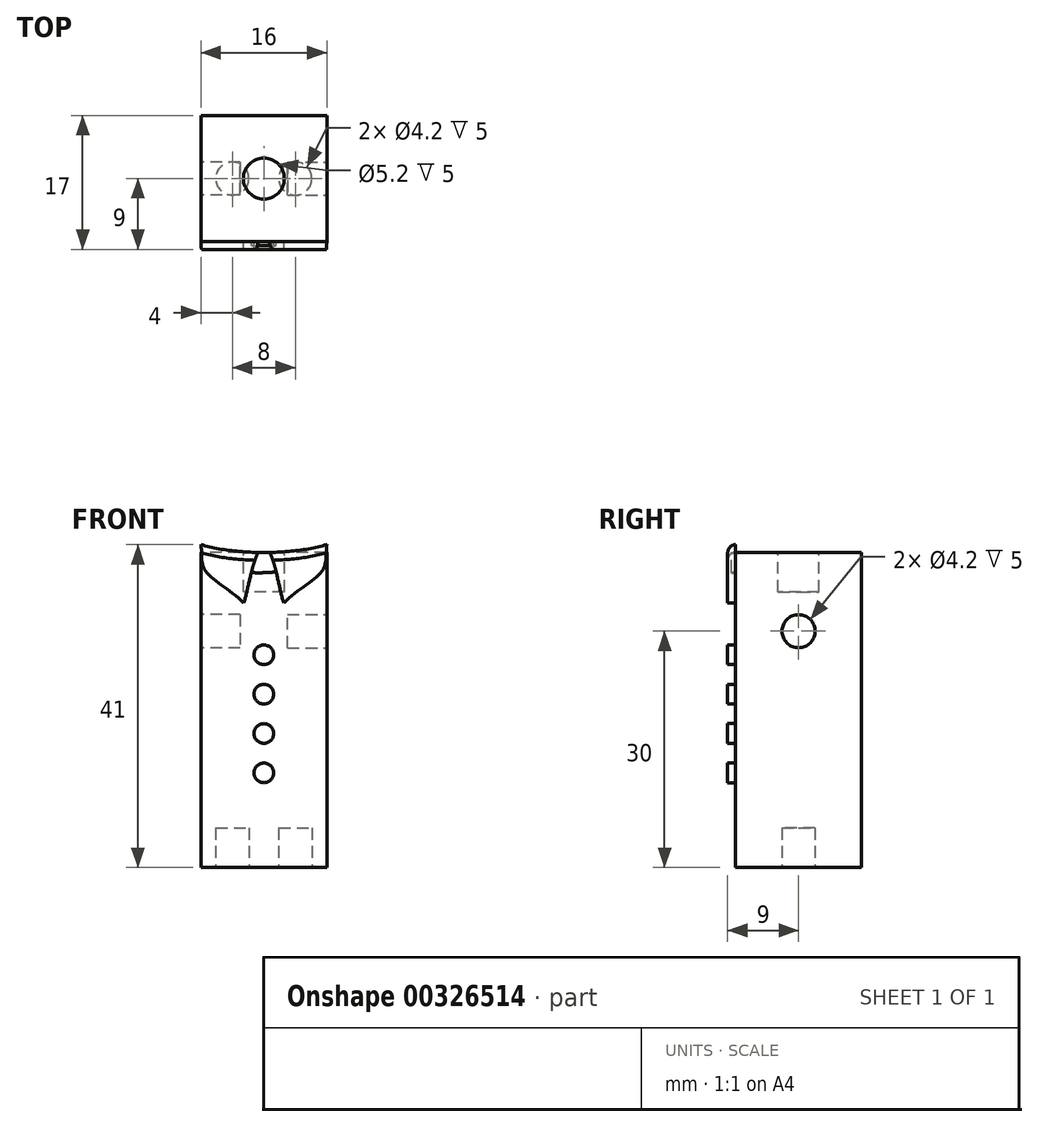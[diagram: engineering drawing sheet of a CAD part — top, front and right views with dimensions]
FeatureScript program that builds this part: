
annotation { "Feature Type Name" : "Feature", "Feature Type Description" : "" }
export const myFeature = defineFeature(function(context is Context, id is Id, definition is map)
    precondition{}
    {
        {
            var Q0;
            Q0=qCreatedBy(makeId("Front.planeOp"),FACE);
            var sketch = newSketch(context, id + "F0", { "sketchPlane" : qUnion([Q0])});
            skLineSegment(sketch, "E0.bottom", {"start": v(8, 20) * mm, "end": v(-8, 20) * mm});
            skLineSegment(sketch, "E0.top", {"start": v(8, -20) * mm, "end": v(-8, -20) * mm});
            skLineSegment(sketch, "E0.left", {"start": v(8, 20) * mm, "end": v(8, -20) * mm});
            skLineSegment(sketch, "E0.right", {"start": v(-8, 20) * mm, "end": v(-8, -20) * mm});
            skPoint(sketch, "E0.middle", {"position": v(0, 0) * mm});
            skSolve(sketch);
        }
        {
            var Q0;
            Q0=makeQuery(id+"F0.imprint","IMPRINT",FACE,{"disambiguationData":[TD([[makeQuery(id+"F0.imprint","IMPRINT",EDGE,{"derivedFrom":sQuery(id+"F0.wireOp",EDGE,"E0.bottom")}),1.0]])]});
            extrude(context, id + "F1", {"entities" : qUnion([Q0]), "depth" : 16 * mm});
        }
        {
            var Q0;
            Q0=makeQuery(id+"F1.opExtrude","SWEPT_FACE",FACE,{"disambiguationData":[OSD([sQuery(id+"F0.wireOp",EDGE,"E0.bottom")])]});
            var sketch = newSketch(context, id + "F2", { "sketchPlane" : qUnion([Q0])});
            skCircle(sketch, "E1", {"center": v(0, -8) * mm, "radius": 2.6 * mm});
            skSolve(sketch);
        }
        {
            var Q0;
            Q0=makeQuery(id+"F2.imprint","IMPRINT",FACE,{"disambiguationData":[TD([[makeQuery(id+"F2.imprint","IMPRINT",EDGE,{"derivedFrom":sQuery(id+"F2.wireOp",EDGE,"E1")}),1.0]])]});
            extrude(context, id + "F3", {"entities" : qUnion([Q0]), "operationType" : NewBodyOperationType.REMOVE, "oppositeDirection" : true, "depth" : 5 * mm});
        }
        {
            var Q0;
            Q0=makeQuery(id+"F1.opExtrude","SWEPT_FACE",FACE,{"disambiguationData":[OSD([sQuery(id+"F0.wireOp",EDGE,"E0.left")])]});
            var sketch = newSketch(context, id + "F4", { "sketchPlane" : qUnion([Q0])});
            skCircle(sketch, "E2", {"center": v(-8, 10) * mm, "radius": 2.1 * mm});
            skSolve(sketch);
        }
        {
            var Q0;
            Q0=makeQuery(id+"F4.imprint","IMPRINT",FACE,{"disambiguationData":[TD([[makeQuery(id+"F4.imprint","IMPRINT",EDGE,{"derivedFrom":sQuery(id+"F4.wireOp",EDGE,"E2")}),1.0]])]});
            extrude(context, id + "F5", {"entities" : qUnion([Q0]), "operationType" : NewBodyOperationType.REMOVE, "oppositeDirection" : true, "depth" : 5 * mm});
        }
        {
            var Q0;
            Q0=makeQuery(id+"F1.opExtrude","SWEPT_FACE",FACE,{"disambiguationData":[OSD([sQuery(id+"F0.wireOp",EDGE,"E0.right")])]});
            var sketch = newSketch(context, id + "F6", { "sketchPlane" : qUnion([Q0])});
            skCircle(sketch, "E3", {"center": v(8, 10) * mm, "radius": 2.1 * mm});
            skSolve(sketch);
        }
        {
            var Q0;
            Q0=makeQuery(id+"F6.imprint","IMPRINT",FACE,{"disambiguationData":[TD([[makeQuery(id+"F6.imprint","IMPRINT",EDGE,{"derivedFrom":sQuery(id+"F6.wireOp",EDGE,"E3")}),1.0]])]});
            extrude(context, id + "F7", {"entities" : qUnion([Q0]), "operationType" : NewBodyOperationType.REMOVE, "oppositeDirection" : true, "depth" : 5 * mm});
        }
        {
            var Q0;
            Q0=makeQuery(id+"F1.opExtrude","SWEPT_FACE",FACE,{"disambiguationData":[OSD([sQuery(id+"F0.wireOp",EDGE,"E0.top")])]});
            var sketch = newSketch(context, id + "F8", { "sketchPlane" : qUnion([Q0])});
            skCircle(sketch, "E4", {"center": v(4, 8) * mm, "radius": 2.1 * mm});
            skSolve(sketch);
        }
        {
            var Q0;
            Q0=makeQuery(id+"F8.imprint","IMPRINT",FACE,{"disambiguationData":[TD([[makeQuery(id+"F8.imprint","IMPRINT",EDGE,{"derivedFrom":sQuery(id+"F8.wireOp",EDGE,"E4")}),1.0]])]});
            extrude(context, id + "F9", {"entities" : qUnion([Q0]), "operationType" : NewBodyOperationType.REMOVE, "oppositeDirection" : true, "depth" : 5 * mm});
        }
        {
            var Q0;
            Q0=makeQuery(id+"F1.opExtrude","SWEPT_FACE",FACE,{"disambiguationData":[OSD([sQuery(id+"F0.wireOp",EDGE,"E0.top")])]});
            var sketch = newSketch(context, id + "F10", { "sketchPlane" : qUnion([Q0])});
            skCircle(sketch, "E5", {"center": v(-4, 8) * mm, "radius": 2.1 * mm});
            skSolve(sketch);
        }
        {
            var Q0;
            Q0=makeQuery(id+"F10.imprint","IMPRINT",FACE,{"disambiguationData":[TD([[makeQuery(id+"F10.imprint","IMPRINT",EDGE,{"derivedFrom":sQuery(id+"F10.wireOp",EDGE,"E5")}),1.0]])]});
            extrude(context, id + "F11", {"entities" : qUnion([Q0]), "operationType" : NewBodyOperationType.REMOVE, "oppositeDirection" : true, "depth" : 5 * mm});
        }
        {
            var Q0;
            Q0=makeQuery(id+"F1.opExtrude","CAP_FACE",FACE,{"disambiguationData":[OSD([sQuery(id+"F0.wireOp",EDGE,"E0.bottom"),sQuery(id+"F0.wireOp",EDGE,"E0.top"),sQuery(id+"F0.wireOp",EDGE,"E0.left"),sQuery(id+"F0.wireOp",EDGE,"E0.right")])],"isStart":false});
            var sketch = newSketch(context, id + "F12", { "sketchPlane" : qUnion([Q0])});
            skCircle(sketch, "E6", {"center": v(0, 7) * mm, "radius": 1.25 * mm});
            skSolve(sketch);
        }
        {
            var Q0;
            Q0=makeQuery(id+"F12.imprint","IMPRINT",FACE,{"disambiguationData":[TD([[makeQuery(id+"F12.imprint","IMPRINT",EDGE,{"derivedFrom":sQuery(id+"F12.wireOp",EDGE,"E6")}),1.0]])]});
            extrude(context, id + "F13", {"entities" : qUnion([Q0]), "operationType" : NewBodyOperationType.ADD, "depth" : 1 * mm});
        }
        {
            var Q0;
            Q0=makeQuery(id+"F1.opExtrude","CAP_FACE",FACE,{"disambiguationData":[OSD([sQuery(id+"F0.wireOp",EDGE,"E0.bottom"),sQuery(id+"F0.wireOp",EDGE,"E0.top"),sQuery(id+"F0.wireOp",EDGE,"E0.left"),sQuery(id+"F0.wireOp",EDGE,"E0.right")])],"isStart":false});
            var sketch = newSketch(context, id + "F14", { "sketchPlane" : qUnion([Q0])});
            skCircle(sketch, "E7", {"center": v(0, 2) * mm, "radius": 1.25 * mm});
            skSolve(sketch);
        }
        {
            var Q0;
            Q0=makeQuery(id+"F14.imprint","IMPRINT",FACE,{"disambiguationData":[TD([[makeQuery(id+"F14.imprint","IMPRINT",EDGE,{"derivedFrom":sQuery(id+"F14.wireOp",EDGE,"E7")}),1.0]])]});
            extrude(context, id + "F15", {"entities" : qUnion([Q0]), "operationType" : NewBodyOperationType.ADD, "depth" : 1 * mm});
        }
        {
            var Q0;
            Q0=makeQuery(id+"F1.opExtrude","CAP_FACE",FACE,{"disambiguationData":[OSD([sQuery(id+"F0.wireOp",EDGE,"E0.bottom"),sQuery(id+"F0.wireOp",EDGE,"E0.top"),sQuery(id+"F0.wireOp",EDGE,"E0.left"),sQuery(id+"F0.wireOp",EDGE,"E0.right")])],"isStart":false});
            var sketch = newSketch(context, id + "F16", { "sketchPlane" : qUnion([Q0])});
            skCircle(sketch, "E8", {"center": v(0, -3) * mm, "radius": 1.25 * mm});
            skSolve(sketch);
        }
        {
            var Q0;
            Q0=makeQuery(id+"F16.imprint","IMPRINT",FACE,{"disambiguationData":[TD([[makeQuery(id+"F16.imprint","IMPRINT",EDGE,{"derivedFrom":sQuery(id+"F16.wireOp",EDGE,"E8")}),1.0]])]});
            extrude(context, id + "F17", {"entities" : qUnion([Q0]), "operationType" : NewBodyOperationType.ADD, "depth" : 1 * mm});
        }
        {
            var Q0;
            Q0=makeQuery(id+"F1.opExtrude","CAP_FACE",FACE,{"disambiguationData":[OSD([sQuery(id+"F0.wireOp",EDGE,"E0.bottom"),sQuery(id+"F0.wireOp",EDGE,"E0.top"),sQuery(id+"F0.wireOp",EDGE,"E0.left"),sQuery(id+"F0.wireOp",EDGE,"E0.right")])],"isStart":false});
            var sketch = newSketch(context, id + "F18", { "sketchPlane" : qUnion([Q0])});
            skCircle(sketch, "E9", {"center": v(0, -8) * mm, "radius": 1.25 * mm});
            skSolve(sketch);
        }
        {
            var Q0;
            Q0=makeQuery(id+"F18.imprint","IMPRINT",FACE,{"disambiguationData":[TD([[makeQuery(id+"F18.imprint","IMPRINT",EDGE,{"derivedFrom":sQuery(id+"F18.wireOp",EDGE,"E9")}),1.0]])]});
            extrude(context, id + "F19", {"entities" : qUnion([Q0]), "operationType" : NewBodyOperationType.ADD, "depth" : 1 * mm});
        }
        {
            var Q0;
            Q0=makeQuery(id+"F1.opExtrude","CAP_FACE",FACE,{"disambiguationData":[OSD([sQuery(id+"F0.wireOp",EDGE,"E0.bottom"),sQuery(id+"F0.wireOp",EDGE,"E0.top"),sQuery(id+"F0.wireOp",EDGE,"E0.left"),sQuery(id+"F0.wireOp",EDGE,"E0.right")])],"isStart":false});
            var sketch = newSketch(context, id + "F20", { "sketchPlane" : qUnion([Q0])});
            skFitSpline(sketch, "E10", {"points": [v(-8, 21) * mm, v(8, 21) * mm], "startDerivative": vector(13.44, -4) * mm, "endDerivative": vector(13.65, 4.05) * mm});
            skFitSpline(sketch, "E11", {"points": [v(-8, 21) * mm, v(-7.6, 17.96) * mm, v(-2.55, 13.56) * mm], "startDerivative": vector(1.28, -6.23) * mm, "endDerivative": vector(8.93, -9.49) * mm});
            skFitSpline(sketch, "E12", {"points": [v(-2.55, 13.56) * mm, v(-0.75, 20) * mm], "startDerivative": vector(1.8, 6.04) * mm, "endDerivative": vector(2.7, 6.14) * mm});
            skFitSpline(sketch, "E13", {"points": [v(8, 21) * mm, v(7.59, 17.96) * mm, v(2.55, 13.56) * mm], "startDerivative": vector(-1.33, -6.24) * mm, "endDerivative": vector(-8.37, -9.42) * mm});
            skFitSpline(sketch, "E14", {"points": [v(2.55, 13.56) * mm, v(0.75, 20) * mm], "startDerivative": vector(-2.09, 6.11) * mm, "endDerivative": vector(-2.78, 5.88) * mm});
            skFitSpline(sketch, "E15", {"points": [v(-1.59, 17.47) * mm, v(1.57, 17.52) * mm], "startDerivative": vector(2.83, -0.35) * mm, "endDerivative": vector(2.9, 0.15) * mm});
            skPoint(sketch, "E16.centerSnap0", {"position": v(0, 20) * mm});
            skPoint(sketch, "E17", {"position": v(7.93, 20) * mm});
            skSolve(sketch);
        }
        {
            var Q0;
            {var subQ0=sQuery(id+"F20.wireOp",EDGE,"E13");var subQ1=sQuery(id+"F20.wireOp",EDGE,"E10");var subQ2=makeQuery(id+"F20.imprint","INTERSECT",VERTEX,{"derivedFrom":[subQ1,subQ0]});Q0=makeQuery(id+"F20.imprint","IMPRINT",FACE,{"disambiguationData":[TD([[makeQuery(id+"F20.imprint","IMPRINT",EDGE,{"disambiguationData":[TD([[subQ2,-1.0]])],"derivedFrom":subQ0}),-1.0]])]});}
            var Q1;
            {var subQ0=sQuery(id+"F20.wireOp",EDGE,"E11");var subQ1=sQuery(id+"F20.wireOp",EDGE,"E10");var subQ2=makeQuery(id+"F20.imprint","INTERSECT",VERTEX,{"derivedFrom":[subQ1,subQ0]});Q1=makeQuery(id+"F20.imprint","IMPRINT",FACE,{"disambiguationData":[TD([[makeQuery(id+"F20.imprint","IMPRINT",EDGE,{"disambiguationData":[TD([[subQ2,-1.0]])],"derivedFrom":subQ0}),1.0]])]});}
            var Q2;
            {var subQ0=sQuery(id+"F20.wireOp",EDGE,"E14");var subQ1=sQuery(id+"F20.wireOp",EDGE,"E13");var subQ2=makeQuery(id+"F20.imprint","INTERSECT",VERTEX,{"derivedFrom":[subQ1,subQ0]});Q2=makeQuery(id+"F20.imprint","IMPRINT",FACE,{"disambiguationData":[TD([[makeQuery(id+"F20.imprint","IMPRINT",EDGE,{"disambiguationData":[TD([[subQ2,1.0]])],"derivedFrom":subQ1}),-1.0]])]});}
            var Q3;
            {var subQ0=sQuery(id+"F20.wireOp",EDGE,"E12");var subQ1=sQuery(id+"F20.wireOp",EDGE,"E11");var subQ2=makeQuery(id+"F20.imprint","INTERSECT",VERTEX,{"derivedFrom":[subQ1,subQ0]});Q3=makeQuery(id+"F20.imprint","IMPRINT",FACE,{"disambiguationData":[TD([[makeQuery(id+"F20.imprint","IMPRINT",EDGE,{"disambiguationData":[TD([[subQ2,1.0]])],"derivedFrom":subQ1}),1.0]])]});}
            extrude(context, id + "F21", {"entities" : qUnion([Q0, Q1, Q2, Q3]), "operationType" : NewBodyOperationType.ADD, "depth" : 1 * mm});
        }
        {
            var Q0;
            {var subQ0=sQuery(id+"F20.wireOp",EDGE,"E10");Q0=makeQuery(id+"F21.opExtrude","CAP_EDGE",EDGE,{"disambiguationData":[OSD([subQ0]),TDD([makeQuery(id+"F20.imprint","IMPRINT",EDGE,{"disambiguationData":[TD([[makeQuery(id+"F20.imprint","INTERSECT",VERTEX,{"derivedFrom":[subQ0,sQuery(id+"F20.wireOp",EDGE,"E11")]}),-1.0],[makeQuery(id+"F20.imprint","INTERSECT",VERTEX,{"derivedFrom":[makeQuery(id+"F1.opExtrude","CAP_EDGE",EDGE,{"disambiguationData":[OSD([sQuery(id+"F0.wireOp",EDGE,"E0.bottom")])],"isStart":false}),subQ0,sQuery(id+"F20.wireOp",EDGE,"E12")]}),1.0]])],"derivedFrom":subQ0})])],"isStart":false});}
            var Q1;
            {var subQ0=sQuery(id+"F20.wireOp",EDGE,"E10");Q1=makeQuery(id+"F21.opExtrude","CAP_EDGE",EDGE,{"disambiguationData":[OSD([subQ0]),TDD([makeQuery(id+"F20.imprint","IMPRINT",EDGE,{"disambiguationData":[TD([[makeQuery(id+"F20.imprint","INTERSECT",VERTEX,{"derivedFrom":[subQ0,sQuery(id+"F20.wireOp",EDGE,"E13")]}),1.0],[makeQuery(id+"F20.imprint","INTERSECT",VERTEX,{"derivedFrom":[makeQuery(id+"F1.opExtrude","CAP_EDGE",EDGE,{"disambiguationData":[OSD([sQuery(id+"F0.wireOp",EDGE,"E0.bottom")])],"isStart":false}),subQ0,sQuery(id+"F20.wireOp",EDGE,"E14")]}),-1.0]])],"derivedFrom":subQ0})])],"isStart":false});}
            fillet(context, id + "F22", {"entities" : qUnion([Q0, Q1]), "radius" : 1 * mm, "tangentPropagation" : true, "allowEdgeOverflow" : false});
        }
        {
            var Q0;
            {var subQ6=sQuery(id+"F20.wireOp",EDGE,"E15");Q0=makeQuery(id+"F20.imprint","IMPRINT",FACE,{"disambiguationData":[TD([[makeQuery(id+"F20.imprint","IMPRINT",EDGE,{"derivedFrom":subQ6}),1.0]])]});}
            extrude(context, id + "F23", {"entities" : qUnion([Q0]), "operationType" : NewBodyOperationType.ADD, "depth" : 0.5 * mm});
        }
    });
